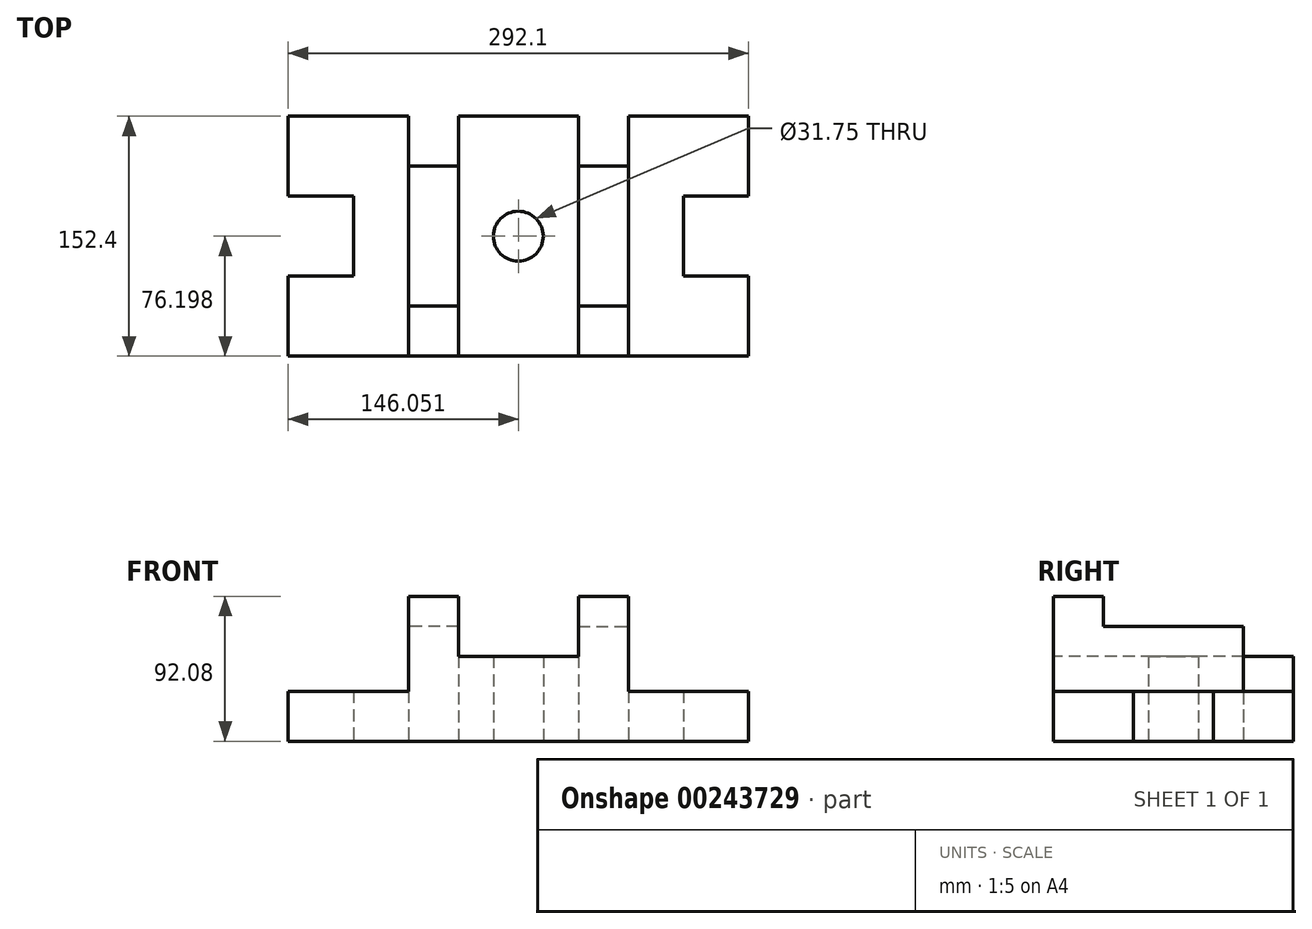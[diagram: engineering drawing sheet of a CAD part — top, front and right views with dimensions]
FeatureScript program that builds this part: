
annotation { "Feature Type Name" : "Feature", "Feature Type Description" : "" }
export const myFeature = defineFeature(function(context is Context, id is Id, definition is map)
    precondition{}
    {
        {
            var Q0;
            Q0=qCreatedBy(makeId("Top.planeOp"),FACE);
            var sketch = newSketch(context, id + "F0", { "sketchPlane" : qUnion([Q0])});
            skLineSegment(sketch, "E0.top", {"start": v(-37.56, 117.09) * mm, "end": v(32.3, 117.09) * mm});
            skLineSegment(sketch, "E0.right", {"start": v(108.5, 66.29) * mm, "end": v(108.5, 117.09) * mm});
            skLineSegment(sketch, "E1.bottom", {"start": v(108.5, 15.49) * mm, "end": v(67.22, 15.49) * mm});
            skLineSegment(sketch, "E1.top", {"start": v(108.5, 66.29) * mm, "end": v(67.22, 66.29) * mm});
            skLineSegment(sketch, "E1.right", {"start": v(67.22, 15.49) * mm, "end": v(67.22, 66.29) * mm});
            skLineSegment(sketch, "E2.bottom", {"start": v(32.3, 117.09) * mm, "end": v(0.54, 117.09) * mm});
            skLineSegment(sketch, "E2.top", {"start": v(32.3, -35.31) * mm, "end": v(0.54, -35.31) * mm});
            skLineSegment(sketch, "E2.left", {"start": v(32.3, 117.09) * mm, "end": v(32.3, -35.31) * mm});
            skLineSegment(sketch, "E2.right", {"start": v(0.54, 117.09) * mm, "end": v(0.54, -35.31) * mm});
            skLineSegment(sketch, "E3.bottom", {"start": v(0.54, 117.09) * mm, "end": v(32.3, 117.09) * mm});
            skLineSegment(sketch, "E3.top", {"start": v(0.54, 85.34) * mm, "end": v(32.3, 85.34) * mm});
            skLineSegment(sketch, "E3.left", {"start": v(0.54, 117.09) * mm, "end": v(0.54, 85.34) * mm});
            skLineSegment(sketch, "E3.right", {"start": v(32.3, 117.09) * mm, "end": v(32.3, 85.34) * mm});
            skLineSegment(sketch, "E4.left", {"start": v(0.54, -35.31) * mm, "end": v(0.54, 15.49) * mm});
            skLineSegment(sketch, "E4.right", {"start": v(32.3, -16.26) * mm, "end": v(32.3, 15.49) * mm});
            skLineSegment(sketch, "E5", {"start": v(32.3, -3.56) * mm, "end": v(0.54, -3.56) * mm});
            skLineSegment(sketch, "E6", {"start": v(108.5, -35.31) * mm, "end": v(108.5, 15.49) * mm});
            skLineSegment(sketch, "E7", {"start": v(32.3, -3.56) * mm, "end": v(32.3, -35.31) * mm});
            skLineSegment(sketch, "E8", {"start": v(32.3, -35.31) * mm, "end": v(108.5, -35.31) * mm});
            skLineSegment(sketch, "E9", {"start": v(32.3, 85.34) * mm, "end": v(32.3, 117.09) * mm});
            skLineSegment(sketch, "E10", {"start": v(32.3, 117.09) * mm, "end": v(108.5, 117.09) * mm});
            skLineSegment(sketch, "E11.trimOffspring", {"start": v(0.54, -35.31) * mm, "end": v(32.3, -35.31) * mm});
            skLineSegment(sketch, "E12", {"start": v(0.54, -35.31) * mm, "end": v(-37.56, -35.31) * mm});
            skLineSegment(sketch, "E13", {"start": v(-37.56, -35.31) * mm, "end": v(-37.56, 25.01) * mm});
            skArc(sketch, "E14", {"start": v(-37.56, 25.01) * mm, "mid": v(-21.68, 40.89) * mm, "end": v(-37.56, 56.76) * mm});
            skLineSegment(sketch, "E15.trimOffspring", {"start": v(-37.56, 56.76) * mm, "end": v(-37.56, 117.09) * mm});
            skSolve(sketch);
        }
        {
            var Q0;
            {var subQ8=sQuery(id+"F0.wireOp",EDGE,"E1.bottom");Q0=makeQuery(id+"F0.imprint","IMPRINT",FACE,{"disambiguationData":[TD([[makeQuery(id+"F0.imprint","IMPRINT",EDGE,{"derivedFrom":subQ8}),1.0]])]});}
            extrude(context, id + "F1", {"entities" : qUnion([Q0]), "depth" : 31.75 * mm});
        }
        {
            var Q0;
            {var subQ8=sQuery(id+"F0.wireOp",EDGE,"E2.right");Q0=makeQuery(id+"F0.imprint","IMPRINT",FACE,{"disambiguationData":[TD([[makeQuery(id+"F0.imprint","IMPRINT",EDGE,{"derivedFrom":subQ8}),-1.0]])]});}
            extrude(context, id + "F2", {"entities" : qUnion([Q0]), "operationType" : NewBodyOperationType.ADD, "depth" : 53.97 * mm});
        }
        {
            var Q0;
            {var subQ1=sQuery(id+"F0.wireOp",EDGE,"E2.right");Q0=makeQuery(id+"F0.imprint","IMPRINT",FACE,{"disambiguationData":[TD([[makeQuery(id+"F0.imprint","IMPRINT",EDGE,{"derivedFrom":subQ1}),1.0]])]});}
            extrude(context, id + "F3", {"entities" : qUnion([Q0]), "operationType" : NewBodyOperationType.ADD, "depth" : 73.02 * mm});
        }
        {
            var Q0;
            {var subQ3=sQuery(id+"F0.wireOp",EDGE,"E5");Q0=makeQuery(id+"F0.imprint","IMPRINT",FACE,{"disambiguationData":[TD([[makeQuery(id+"F0.imprint","IMPRINT",EDGE,{"derivedFrom":subQ3}),1.0]])]});}
            var Q1;
            Q1=makeQuery(id+"F0.imprint","IMPRINT",FACE,{"disambiguationData":[TD([[makeQuery(id+"F0.imprint","IMPRINT",EDGE,{"derivedFrom":sQuery(id+"F0.wireOp",EDGE,"E3.bottom")}),-1.0]])]});
            extrude(context, id + "F4", {"entities" : qUnion([Q0, Q1]), "operationType" : NewBodyOperationType.ADD, "depth" : 92.07 * mm});
        }
        {
            var Q0;
            {var subQ1=sQuery(id+"F0.wireOp",EDGE,"E2.right");Q0=makeQuery(id+"F0.imprint","IMPRINT",FACE,{"disambiguationData":[TD([[makeQuery(id+"F0.imprint","IMPRINT",EDGE,{"derivedFrom":subQ1}),1.0]])]});}
            extrude(context, id + "F5", {"entities" : qUnion([Q0]), "operationType" : NewBodyOperationType.ADD, "depth" : 73.02 * mm});
        }
        {
            var Q0;
            Q0=makeQuery(id+"F1.opExtrude","SWEPT_BODY",BODY,{"disambiguationData":[OSD([sQuery(id+"F0.wireOp",EDGE,"E0.bottom"),sQuery(id+"F0.wireOp",EDGE,"E0.top"),sQuery(id+"F0.wireOp",EDGE,"E0.right"),sQuery(id+"F0.wireOp",EDGE,"E1.bottom"),sQuery(id+"F0.wireOp",EDGE,"E1.top"),sQuery(id+"F0.wireOp",EDGE,"E1.right"),sQuery(id+"F0.wireOp",EDGE,"E2.left"),sQuery(id+"F0.wireOp",EDGE,"E3.right"),sQuery(id+"F0.wireOp",EDGE,"E4.right")])]});
            var Q1;
            Q1=makeQuery(id+"F2.opExtrude","SWEPT_FACE",FACE,{"disambiguationData":[OSD([sQuery(id+"F0.wireOp",EDGE,"E15.trimOffspring")])]});
            mirror(context, id + "F6", {"operationType" : NewBodyOperationType.ADD, "entities" : qUnion([Q0]), "mirrorPlane" : qUnion([Q1])});
        }
    });
